# Revit family: Triatek_EcoAir-Rect. (Dual & Triple)_Valve-Revit 2020-R0
name_source: partatom
category: Duct Accessories
units: mm (PartAtom-declared; Revit-internal decimal feet)

## family parameters
Always vertical = Yes
Cut with Voids When Loaded = Yes
OmniClass Number = 23.75.65.14.14.17
OmniClass Title = Flow Controls
Part Type = Damper
Round Connector Dimension = Use Diameter
Shared = No
Work Plane-Based = No

## types (3) — shared parameters
08 = No
1 = No
2 way Eco = Yes
3 Way Eco = No
Accuracy = 5% or 10cfm Whichever is greater
Actual Power Factor = 1
Airstream Operating Temperature = 0 F to 122 F (-7.78 C to 50 C)
Ambient Environment Temperature = -22 F to 122  F (-30 C to 50 C)
CFM Command Signal = 0 VDC to 10 VDC with Default Scaling set to 1V=100 CFM
CFM Feedback Signal = 0 VDC to 10 VDC with Default Scaling set to 1V=100 CFM
Connector Description = Rectangular Duct Conector
Controller Material = Paint - Powder - York Blue
D2 = 48.3 "
Description = Ultra-low pressure drop air valve
Design Air Flow = 0 CFM
Design Voltage = 0 V
Dual = Yes
Dual-60 VA = Yes
Failure Modes = FA= Fail to close or open (optimal for critical applications)
Humidity = 0% RH to 90% RH
Input Power = 24 VAC 20% 50Hz/60Hz
Invalid Material = Area - Warning
Manufacturer = Triatek HVAC
Material = Metal - Aluminum - Satin
Model = Eco-Air Valve
Network = BACnet MS/TP
Operating Pressure = 0.01 in W.G. to 10 in W.G. differential pressure across valve
Outer Prevention Material = Metal - Aluminum - Powder Coated - Pearl White
Power Requirements = Dual-60 VA
Round Connector Description = Disabled
Round Distance = 4 "
Round Length = 10 "
Select Unit Type = 1
Shaft and Support Material = Metal - Steel
Show Invalid Model = No
Show Room Tag = No
Show Single Eco = Yes
Single-30 VA = No
Size 8 Visibility = No
Triple = No
Triple- 90 VA = No
Type 2 = Yes
Type 3 = No
URL = https://www.triatek.com
Unit Component Apparent Power = 0 VA
Valve Dia = 1 "
Weight per sq ft = 0.00 lb/ft²
zero-valued in all types: Default Elevation, Distance, Outer Rad

## per-type parameters (varying)
| type | 10 | 12 | 14 | A | B | C | C2 | C3 | Collar Height | Collar Width | Connector Distance | D | D1 | D3 | Dia | Inner Dia | Outer Dia | Select Unit Size | c1 |
| 12 | No | Yes | No | 26.8 " | 16.44 " | 26.75 " | 6.5 " | 6.5 " | 13.5 " | 26.75 " | 26.8 " | 13.5 " | 26.75 " | 17.28 " | 11.68 " | 11.75 " | 12.42 " | 3 | 6.5 " |
| 10 | Yes | No | No | 26 " | 14.45 " | 22.63 " | 5.44 " | 5.44 " | 11.44 " | 22.63 " | 26 " | 11.44 " | 22.63 " | 18.28 " | 9.74 " | 9.75 " | 10.48 " | 2 | 5.44 " |
| 14 | No | No | Yes | 30 " | 18.38 " | 32.15 " | 8.2 " | 8.2 " | 16 " | 32.15 " | 30 " | 16 " | 32.15 " | 16.28 " | 13.62 " | 13.75 " | 14.36 " | 4 | 8.2 " |

## geometry (parser evidence)
native form markers: Sweep x30
no freeform markers — native parametric forms only
